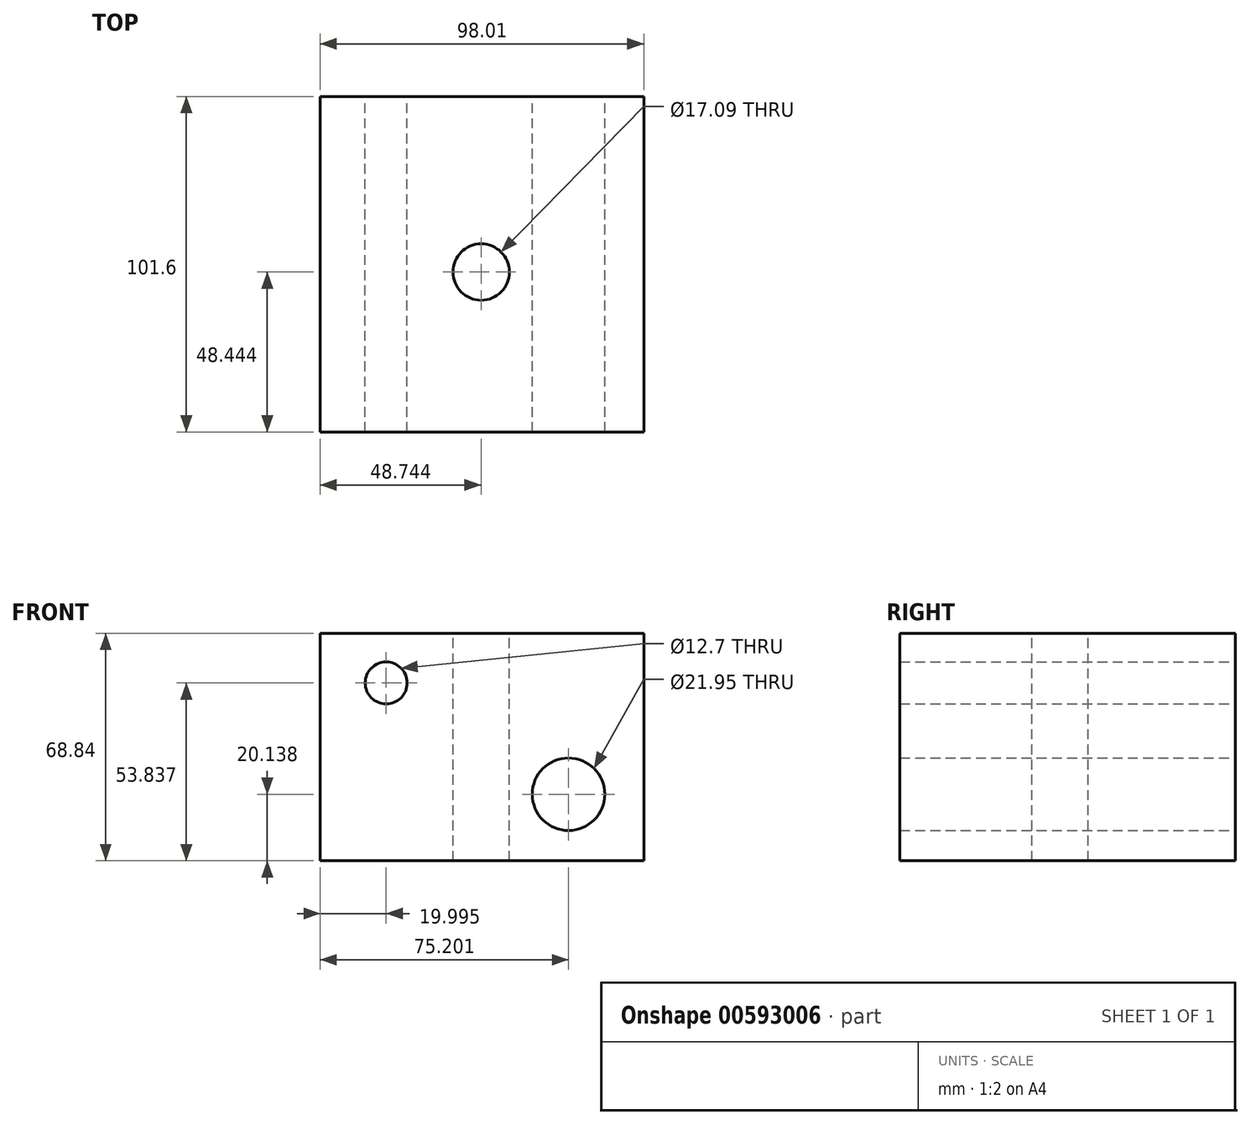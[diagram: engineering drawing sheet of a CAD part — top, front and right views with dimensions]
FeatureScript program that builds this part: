
annotation { "Feature Type Name" : "Feature", "Feature Type Description" : "" }
export const myFeature = defineFeature(function(context is Context, id is Id, definition is map)
    precondition{}
    {
        {
            var Q0;
            Q0=qCreatedBy(makeId("Front.planeOp"),FACE);
            var sketch = newSketch(context, id + "F0", { "sketchPlane" : qUnion([Q0])});
            skLineSegment(sketch, "E0.bottom", {"start": v(-43.84, 36.83) * mm, "end": v(54.17, 36.83) * mm});
            skLineSegment(sketch, "E0.top", {"start": v(-43.84, -32) * mm, "end": v(54.17, -32) * mm});
            skLineSegment(sketch, "E0.left", {"start": v(-43.84, 36.83) * mm, "end": v(-43.84, -32) * mm});
            skLineSegment(sketch, "E0.right", {"start": v(54.17, 36.83) * mm, "end": v(54.17, -32) * mm});
            skCircle(sketch, "E1", {"center": v(-23.84, 21.83) * mm, "radius": 6.35 * mm});
            skCircle(sketch, "E2", {"center": v(31.36, -11.87) * mm, "radius": 10.98 * mm});
            skSolve(sketch);
        }
        {
            var Q0;
            Q0 = qSketchRegion(id + "F0", true);
            extrude(context, id + "F1", {"entities" : qUnion([Q0]), "depth" : 63.5 * mm, "offsetDistance" : 25.4 * mm, "hasSecondDirection" : true, "secondDirectionOppositeDirection" : true, "secondDirectionDepth" : 38.1 * mm});
        }
        {
            var Q0;
            Q0=makeQuery(id+"F1.opExtrude","SWEPT_FACE",FACE,{"disambiguationData":[OSD([sQuery(id+"F0.wireOp",EDGE,"E0.bottom")])]});
            var sketch = newSketch(context, id + "F2", { "sketchPlane" : qUnion([Q0])});
            skCircle(sketch, "E3", {"center": v(4.9, -15.06) * mm, "radius": 8.54 * mm});
            skSolve(sketch);
        }
        {
            var Q0;
            Q0 = qSketchRegion(id + "F2", true);
            extrude(context, id + "F3", {"entities" : qUnion([Q0]), "operationType" : NewBodyOperationType.REMOVE, "endBound" : BoundingType.THROUGH_ALL, "oppositeDirection" : true, "depth" : 25.4 * mm, "offsetDistance" : 25.4 * mm});
        }
    });
